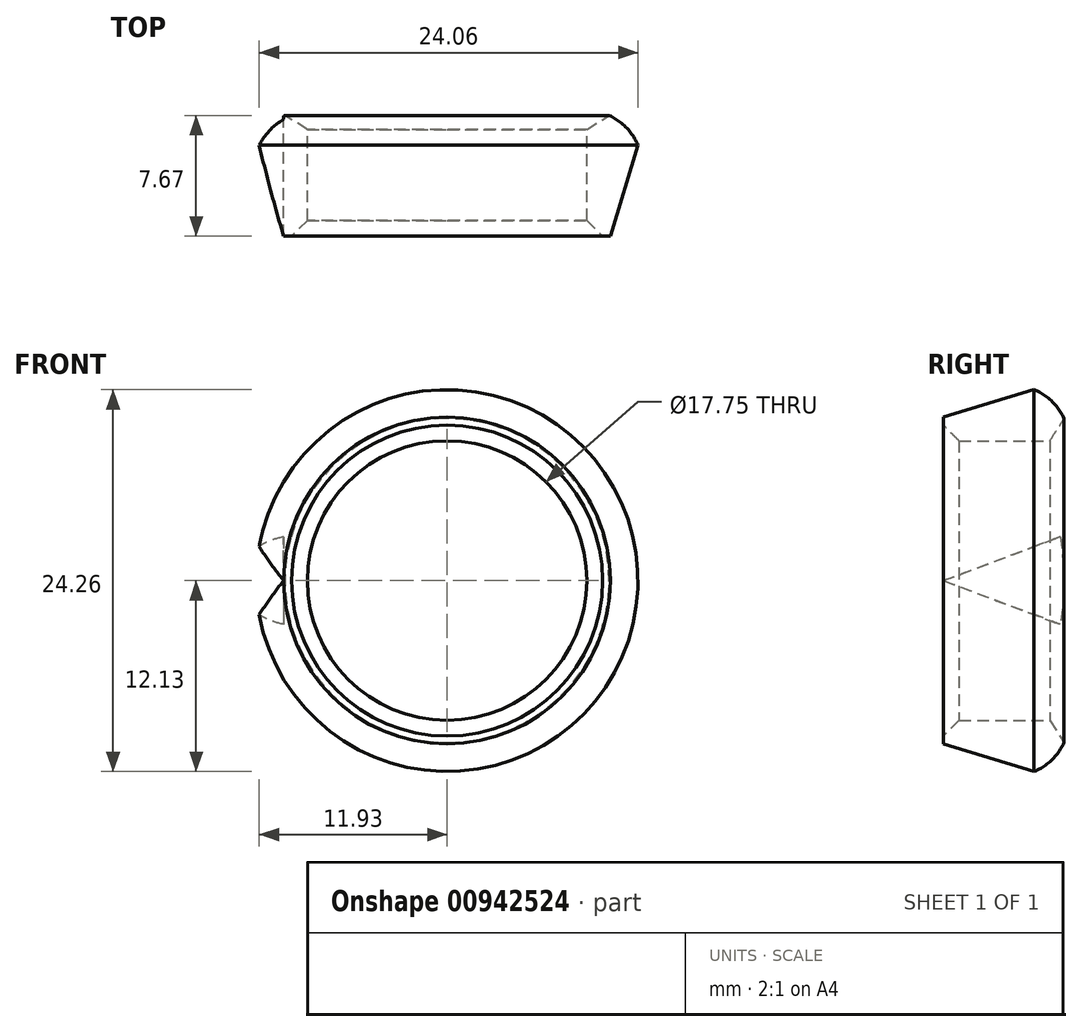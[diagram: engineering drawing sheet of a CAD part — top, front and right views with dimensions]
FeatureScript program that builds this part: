
annotation { "Feature Type Name" : "Feature", "Feature Type Description" : "" }
export const myFeature = defineFeature(function(context is Context, id is Id, definition is map)
    precondition{}
    {
        {
            var Q0;
            Q0=qCreatedBy(makeId("Front.planeOp"),FACE);
            var sketch = newSketch(context, id + "F0", { "sketchPlane" : qUnion([Q0])});
            skCircle(sketch, "E0", {"center": v(0, 0) * mm, "radius": 8.88 * mm});
            skSolve(sketch);
        }
        {
            var Q0;
            Q0=qCreatedBy(makeId("Right.planeOp"),FACE);
            var sketch = newSketch(context, id + "F1", { "sketchPlane" : qUnion([Q0])});
            skLineSegment(sketch, "E1", {"start": v(-4, 8.88) * mm, "end": v(4, 8.88) * mm});
            skPoint(sketch, "E2", {"position": v(0, 8.88) * mm});
            skArc(sketch, "E3", {"start": v(4, 8.88) * mm, "mid": v(3.36, 10.83) * mm, "end": v(1.77, 12.12) * mm});
            skLineSegment(sketch, "E4", {"start": v(-4, 8.88) * mm, "end": v(-4, 10.38) * mm});
            skLineSegment(sketch, "E5", {"start": v(-4, 10.38) * mm, "end": v(1.77, 12.13) * mm});
            skSolve(sketch);
        }
        {
            var Q0;
            Q0=makeQuery(id+"F1.imprint","IMPRINT",FACE,{"disambiguationData":[TD([[makeQuery(id+"F1.imprint","IMPRINT",EDGE,{"derivedFrom":sQuery(id+"F1.wireOp",EDGE,"E1")}),1.0]])]});
            var Q1;
            Q1=sQuery(id+"F0.wireOp",EDGE,"E0");
            revolve(context, id + "F2", {"surfaceOperationType" : NewSurfaceOperationType.NEW, "entities" : qUnion([Q0]), "axis" : qUnion([Q1]), "revolveType" : RevolveType.FULL});
        }
        {
            var Q0;
            Q0=makeQuery(id+"F2.opRevolve","SWEPT_EDGE",EDGE,{"disambiguationData":[OSD([sQuery(id+"F1.wireOp",EDGE,"E1"),sQuery(id+"F1.wireOp",EDGE,"E3")])]});
            var Q1;
            Q1=makeQuery(id+"F2.opRevolve","SWEPT_EDGE",EDGE,{"disambiguationData":[OSD([sQuery(id+"F1.wireOp",EDGE,"E1"),sQuery(id+"F1.wireOp",EDGE,"E4")])]});
            chamfer(context, id + "F3", {"entities" : qUnion([Q0, Q1]), "width" : 1 * mm, "tangentPropagation" : true});
        }
        {
            var Q0;
            Q0=qCreatedBy(makeId("Right.planeOp"),FACE);
            var sketch = newSketch(context, id + "F4", { "sketchPlane" : qUnion([Q0])});
            skLineSegment(sketch, "E6", {"start": v(-4, 0) * mm, "end": v(3.7, 2.88) * mm});
            skLineSegment(sketch, "E7", {"start": v(3.7, 2.88) * mm, "end": v(3.7, 0) * mm});
            skLineSegment(sketch, "E8.MirrorCS", {"start": v(-4, 0) * mm, "end": v(3.7, -2.88) * mm});
            skLineSegment(sketch, "E9.MirrorCS", {"start": v(3.7, -2.88) * mm, "end": v(3.7, 0) * mm});
            skSolve(sketch);
        }
        {
            var Q0;
            Q0=makeQuery(id+"F4.imprint","IMPRINT",FACE,{"disambiguationData":[TD([[makeQuery(id+"F4.imprint","IMPRINT",EDGE,{"derivedFrom":sQuery(id+"F4.wireOp",EDGE,"E6")}),-1.0]])]});
            extrude(context, id + "F5", {"entities" : qUnion([Q0]), "operationType" : NewBodyOperationType.REMOVE, "oppositeDirection" : true, "depth" : 25 * mm, "offsetDistance" : 25 * mm, "hasSecondDirection" : true, "secondDirectionOppositeDirection" : true, "secondDirectionDepth" : ((17.75 / 2) + 1.5) * mm});
        }
    });
